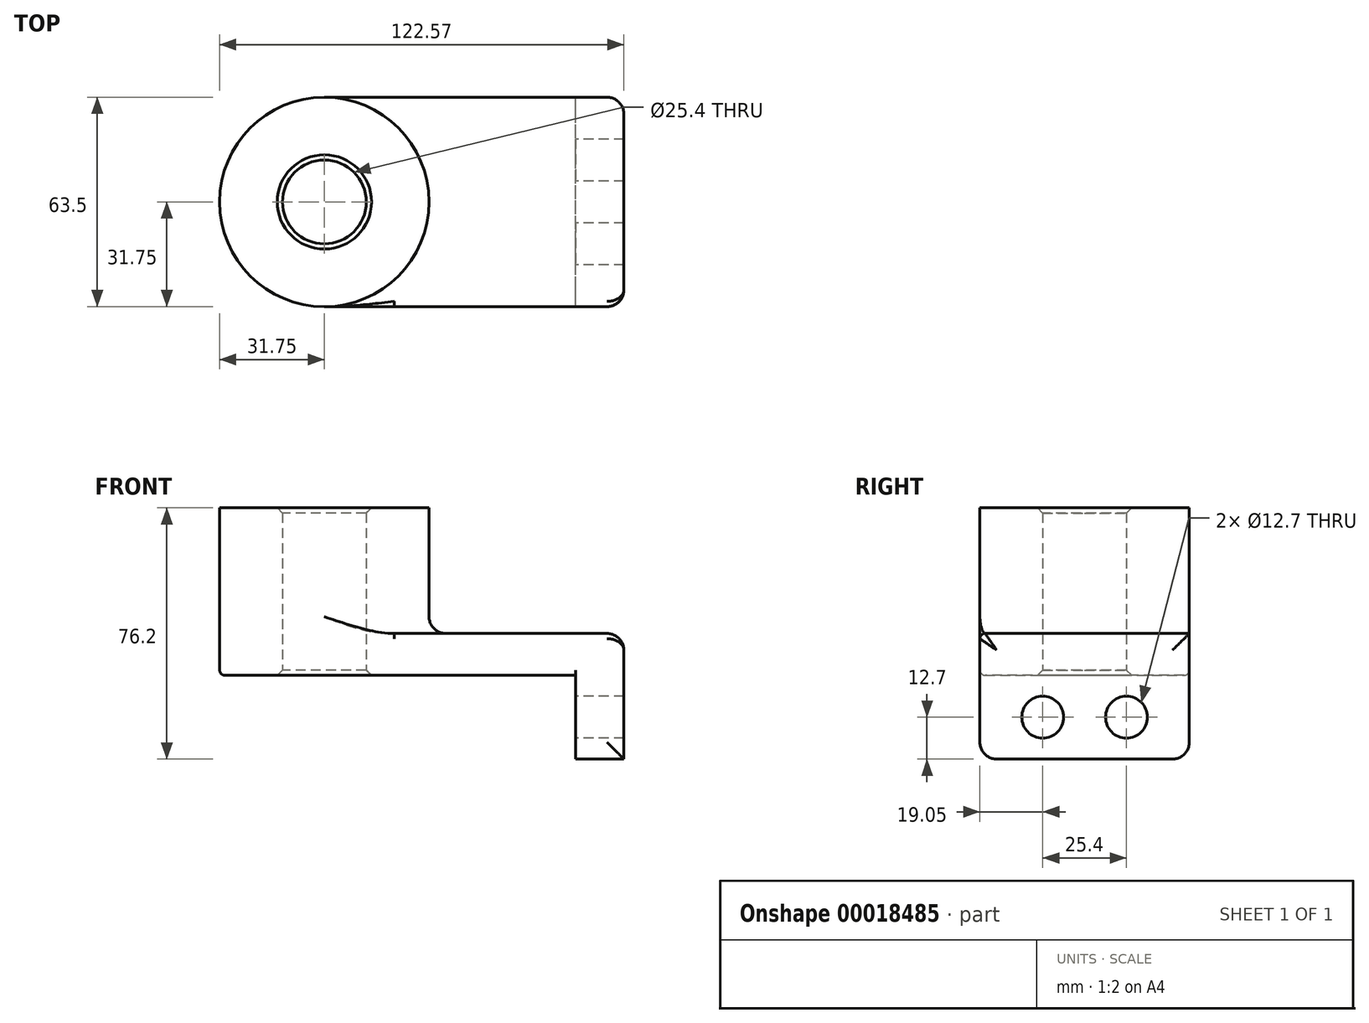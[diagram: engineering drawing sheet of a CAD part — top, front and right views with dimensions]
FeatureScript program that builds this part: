
annotation { "Feature Type Name" : "Feature", "Feature Type Description" : "" }
export const myFeature = defineFeature(function(context is Context, id is Id, definition is map)
    precondition{}
    {
        {
            var Q0;
            Q0=qCreatedBy(makeId("Top.planeOp"),FACE);
            var sketch = newSketch(context, id + "F0", { "sketchPlane" : qUnion([Q0])});
            skLineSegment(sketch, "E0.rect.bottom", {"start": v(38.1, -31.75) * mm, "end": v(-38.1, -31.75) * mm});
            skLineSegment(sketch, "E0.rect.top", {"start": v(38.1, 31.75) * mm, "end": v(-38.1, 31.75) * mm});
            skLineSegment(sketch, "E0.rect.left", {"start": v(38.1, -31.75) * mm, "end": v(38.1, 31.75) * mm});
            skLineSegment(sketch, "E0.rect.right", {"start": v(-38.1, -31.75) * mm, "end": v(-38.1, 31.75) * mm});
            skPoint(sketch, "E0.rect.middle", {"position": v(0, 0) * mm});
            skCircle(sketch, "E1", {"center": v(-38.1, 0) * mm, "radius": 31.75 * mm});
            skCircle(sketch, "E2", {"center": v(-38.1, 0) * mm, "radius": 12.7 * mm});
            skSolve(sketch);
        }
        {
            var Q0;
            Q0 = qSketchRegion(id + "F0", true);
            extrude(context, id + "F1", {"entities" : qUnion([Q0]), "depth" : 12.7 * mm});
        }
        {
            var Q0;
            {var subQ0=sQuery(id+"F0.wireOp",EDGE,"E2");var subQ1=sQuery(id+"F0.wireOp",EDGE,"E0.rect.right");var subQ3=makeQuery(id+"F0.imprint","INTERSECT",VERTEX,{"disambiguationData":[OD(0.0)],"derivedFrom":[subQ1,subQ0]});Q0=makeQuery(id+"F0.imprint","IMPRINT",FACE,{"disambiguationData":[TD([[makeQuery(id+"F0.imprint","IMPRINT",EDGE,{"disambiguationData":[TD([[subQ3,1.0]])],"derivedFrom":subQ0}),-1.0]])]});}
            var Q1;
            {var subQ0=sQuery(id+"F0.wireOp",EDGE,"E2");var subQ1=sQuery(id+"F0.wireOp",EDGE,"E0.rect.right");var subQ3=makeQuery(id+"F0.imprint","INTERSECT",VERTEX,{"disambiguationData":[OD(0.0)],"derivedFrom":[subQ1,subQ0]});Q1=makeQuery(id+"F0.imprint","IMPRINT",FACE,{"disambiguationData":[TD([[makeQuery(id+"F0.imprint","IMPRINT",EDGE,{"disambiguationData":[TD([[subQ3,-1.0]])],"derivedFrom":subQ0}),-1.0]])]});}
            extrude(context, id + "F2", {"entities" : qUnion([Q0, Q1]), "operationType" : NewBodyOperationType.ADD, "depth" : 50.8 * mm});
        }
        {
            var Q0;
            Q0=makeQuery(id+"F1.opExtrude","SWEPT_FACE",FACE,{"disambiguationData":[OSD([sQuery(id+"F0.wireOp",EDGE,"E0.rect.left")])]});
            var sketch = newSketch(context, id + "F3", { "sketchPlane" : qUnion([Q0])});
            skLineSegment(sketch, "E3.bottom", {"start": v(-31.75, 12.7) * mm, "end": v(31.75, 12.7) * mm});
            skLineSegment(sketch, "E3.top", {"start": v(-31.75, -25.4) * mm, "end": v(31.75, -25.4) * mm});
            skLineSegment(sketch, "E3.left", {"start": v(-31.75, 12.7) * mm, "end": v(-31.75, -25.4) * mm});
            skLineSegment(sketch, "E3.right", {"start": v(31.75, 12.7) * mm, "end": v(31.75, -25.4) * mm});
            skCircle(sketch, "E4", {"center": v(-12.7, -12.7) * mm, "radius": 6.35 * mm});
            skLineSegment(sketch, "E5", {"start": v(0, 0) * mm, "end": v(0, -25.4) * mm, "construction": true});
            skCircle(sketch, "E6.MirrorC", {"center": v(12.7, -12.7) * mm, "radius": 6.35 * mm});
            skSolve(sketch);
        }
        {
            var Q0;
            Q0 = qSketchRegion(id + "F3", true);
            extrude(context, id + "F4", {"entities" : qUnion([Q0]), "operationType" : NewBodyOperationType.ADD, "depth" : 14.62 * mm});
        }
        {
            var Q0;
            {var subQ0=sQuery(id+"F0.wireOp",EDGE,"E1");Q0=makeQuery(id+"F2.boolean.opBoolean","INTERSECT",EDGE,{"derivedFrom":[makeQuery(id+"F1.opExtrude","CAP_FACE",FACE,{"disambiguationData":[OSD([sQuery(id+"F0.wireOp",EDGE,"E0.rect.bottom"),sQuery(id+"F0.wireOp",EDGE,"E0.rect.top"),sQuery(id+"F0.wireOp",EDGE,"E0.rect.left"),subQ0,sQuery(id+"F0.wireOp",EDGE,"E2")])],"isStart":false}),makeQuery(id+"F2.opExtrude","SWEPT_FACE",FACE,{"disambiguationData":[OSD([subQ0])]})]});}
            var Q1;
            Q1=makeQuery(id+"F4.opExtrude","CAP_EDGE",EDGE,{"disambiguationData":[OSD([sQuery(id+"F3.wireOp",EDGE,"E3.bottom")])],"isStart":false});
            var Q2;
            Q2=makeQuery(id+"F4.opExtrude","CAP_EDGE",EDGE,{"disambiguationData":[OSD([sQuery(id+"F3.wireOp",EDGE,"E3.left")])],"isStart":false});
            var Q3;
            Q3=makeQuery(id+"F4.opExtrude","SWEPT_EDGE",EDGE,{"disambiguationData":[OSD([sQuery(id+"F3.wireOp",EDGE,"E3.top"),sQuery(id+"F3.wireOp",EDGE,"E3.left")])]});
            var Q4;
            Q4=makeQuery(id+"F4.opExtrude","SWEPT_EDGE",EDGE,{"disambiguationData":[OSD([sQuery(id+"F3.wireOp",EDGE,"E3.top"),sQuery(id+"F3.wireOp",EDGE,"E3.right")])]});
            var Q5;
            Q5=makeQuery(id+"F4.opExtrude","CAP_EDGE",EDGE,{"disambiguationData":[OSD([sQuery(id+"F3.wireOp",EDGE,"E3.right")])],"isStart":false});
            fillet(context, id + "F5", {"entities" : qUnion([Q0, Q1, Q2, Q3, Q4, Q5]), "radius" : 5.08 * mm, "tangentPropagation" : true, "allowEdgeOverflow" : false});
        }
        {
            var Q0;
            Q0=makeQuery(id+"F4.boolean.opBoolean","MERGE",EDGE,{"derivedFrom":[makeQuery(id+"F1.opExtrude","CAP_EDGE",EDGE,{"disambiguationData":[OSD([sQuery(id+"F0.wireOp",EDGE,"E0.rect.bottom")])],"isStart":false}),makeQuery(id+"F4.opExtrude","SWEPT_EDGE",EDGE,{"disambiguationData":[OSD([sQuery(id+"F3.wireOp",EDGE,"E3.bottom"),sQuery(id+"F3.wireOp",EDGE,"E3.left")])]})]});
            var Q1;
            Q1=makeQuery(id+"F1.opExtrude","CAP_EDGE",EDGE,{"disambiguationData":[OSD([sQuery(id+"F0.wireOp",EDGE,"E0.rect.bottom")])],"isStart":true});
            var Q2;
            Q2=makeQuery(id+"F1.opExtrude","CAP_EDGE",EDGE,{"disambiguationData":[OSD([sQuery(id+"F0.wireOp",EDGE,"E0.rect.left")])],"isStart":true});
            fillet(context, id + "F6", {"entities" : qUnion([Q0, Q1, Q2]), "radius" : 1.59 * mm, "tangentPropagation" : true, "allowEdgeOverflow" : false});
        }
        {
            var Q0;
            {var subQ0=sQuery(id+"F0.wireOp",EDGE,"E2");Q0=makeQuery(id+"F2.boolean.opBoolean","MERGE",FACE,{"derivedFrom":[makeQuery(id+"F1.opExtrude","SWEPT_FACE",FACE,{"disambiguationData":[OSD([subQ0])]}),makeQuery(id+"F2.opExtrude","SWEPT_FACE",FACE,{"disambiguationData":[OSD([subQ0])]})]});}
            chamfer(context, id + "F7", {"entities" : qUnion([Q0]), "width" : 1.59 * mm, "tangentPropagation" : true});
        }
    });
